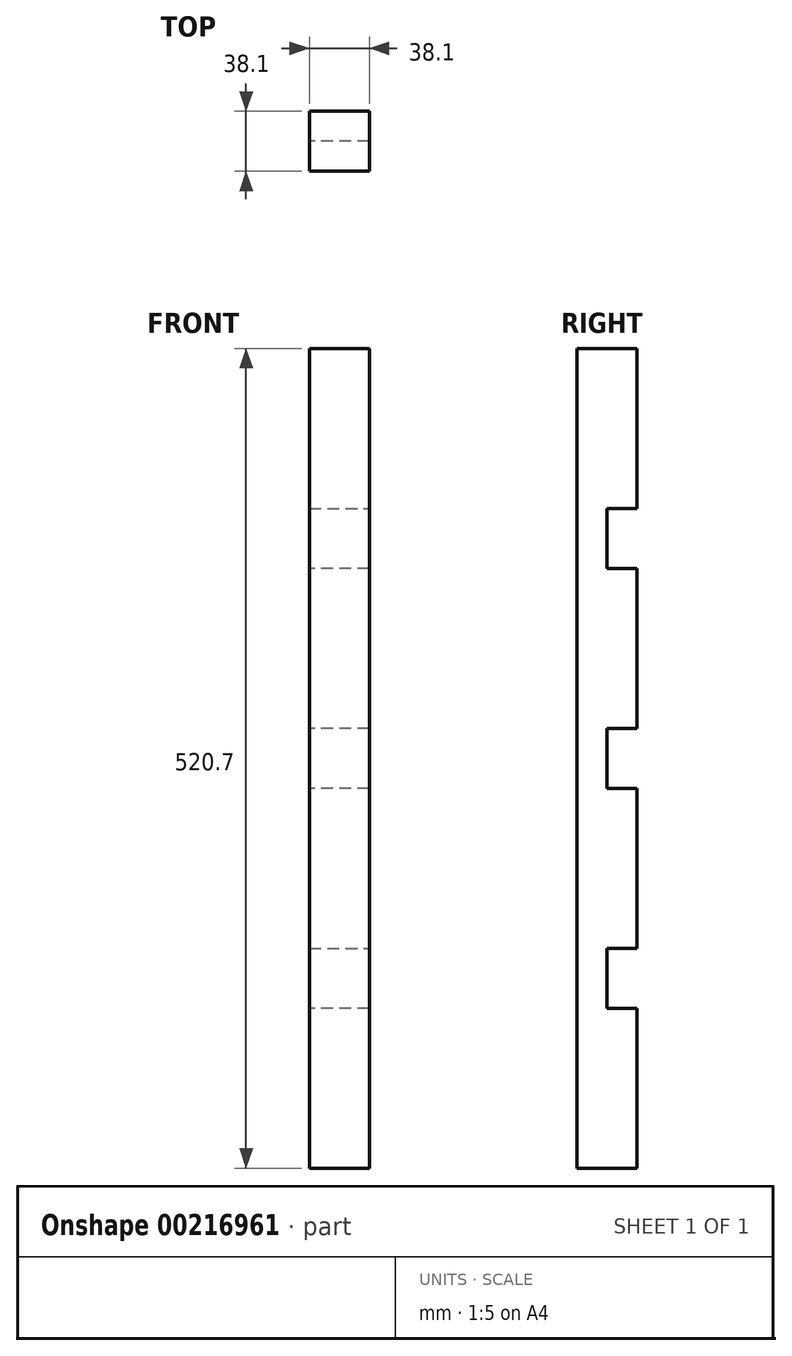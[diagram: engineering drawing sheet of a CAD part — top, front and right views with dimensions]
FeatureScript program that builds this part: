
annotation { "Feature Type Name" : "Feature", "Feature Type Description" : "" }
export const myFeature = defineFeature(function(context is Context, id is Id, definition is map)
    precondition{}
    {
        {
            var Q0;
            Q0=qCreatedBy(makeId("Top.planeOp"),FACE);
            var sketch = newSketch(context, id + "F0", { "sketchPlane" : qUnion([Q0])});
            skLineSegment(sketch, "E0", {"start": v(0, 0) * mm, "end": v(-50.8, 0) * mm});
            skLineSegment(sketch, "E1", {"start": v(0, 0) * mm, "end": v(50.8, 0) * mm});
            skLineSegment(sketch, "E2", {"start": v(50.8, 0) * mm, "end": v(50.8, 38.1) * mm});
            skLineSegment(sketch, "E3", {"start": v(88.9, 38.1) * mm, "end": v(88.9, 0) * mm});
            skLineSegment(sketch, "E4", {"start": v(88.9, 0) * mm, "end": v(190.5, 0) * mm});
            skLineSegment(sketch, "E5", {"start": v(190.5, 0) * mm, "end": v(190.5, 38.1) * mm});
            skLineSegment(sketch, "E6", {"start": v(-50.8, 0) * mm, "end": v(-50.8, 38.1) * mm});
            skLineSegment(sketch, "E7", {"start": v(-88.9, 38.1) * mm, "end": v(-190.5, 38.1) * mm});
            skLineSegment(sketch, "E8", {"start": v(-190.5, 38.1) * mm, "end": v(-190.5, 0) * mm});
            skLineSegment(sketch, "E9", {"start": v(-228.6, 0) * mm, "end": v(-228.6, 38.1) * mm});
            skLineSegment(sketch, "E10", {"start": v(-228.6, 38.1) * mm, "end": v(-330.2, 38.1) * mm});
            skLineSegment(sketch, "E11", {"start": v(-330.2, 38.1) * mm, "end": v(-330.2, 0) * mm});
            skLineSegment(sketch, "E12", {"start": v(-88.9, 0) * mm, "end": v(-88.9, 38.1) * mm});
            skLineSegment(sketch, "E13.trimOffspring", {"start": v(-330.2, 38.1) * mm, "end": v(-228.6, 38.1) * mm});
            skLineSegment(sketch, "E14.trimOffspring", {"start": v(-190.5, 38.1) * mm, "end": v(-88.9, 38.1) * mm});
            skLineSegment(sketch, "E15.trimOffspring", {"start": v(-228.6, 0) * mm, "end": v(-330.2, 0) * mm});
            skLineSegment(sketch, "E16.trimOffspring", {"start": v(-88.9, 0) * mm, "end": v(-190.5, 0) * mm});
            skLineSegment(sketch, "E17.trimOffspring", {"start": v(-50.8, 38.1) * mm, "end": v(50.8, 38.1) * mm});
            skLineSegment(sketch, "E18.trimOffspring", {"start": v(50.8, 0) * mm, "end": v(0, 0) * mm});
            skLineSegment(sketch, "E19.trimOffspring", {"start": v(88.9, 38.1) * mm, "end": v(190.5, 38.1) * mm});
            skLineSegment(sketch, "E20.trimOffspring", {"start": v(190.5, 0) * mm, "end": v(88.9, 0) * mm});
            skLineSegment(sketch, "E21", {"start": v(-88.9, -135.66) * mm, "end": v(-69.85, -135.66) * mm, "construction": true});
            skLineSegment(sketch, "E22", {"start": v(-69.85, -135.66) * mm, "end": v(-69.85, 272.84) * mm, "construction": true});
            skSolve(sketch);
        }
        {
            var Q0;
            Q0=qSketchRegion(id+"F0",true);
            extrude(context, id + "F1", {"entities" : qUnion([Q0]), "depth" : 19.05 * mm});
        }
        {
            var Q0;
            Q0=makeQuery(id+"F1.opExtrude","CAP_FACE",FACE,{"disambiguationData":[OSD([sQuery(id+"F0.wireOp",EDGE,"E9"),sQuery(id+"F0.wireOp",EDGE,"E11"),sQuery(id+"F0.wireOp",EDGE,"E13.trimOffspring"),sQuery(id+"F0.wireOp",EDGE,"E15.trimOffspring")])],"isStart":false});
            var sketch = newSketch(context, id + "F2", { "sketchPlane" : qUnion([Q0])});
            skLineSegment(sketch, "E23.bottom", {"start": v(-330.2, 0) * mm, "end": v(190.5, 0) * mm});
            skLineSegment(sketch, "E23.top", {"start": v(-330.2, 38.1) * mm, "end": v(190.5, 38.1) * mm});
            skLineSegment(sketch, "E23.left", {"start": v(-330.2, 0) * mm, "end": v(-330.2, 38.1) * mm});
            skLineSegment(sketch, "E23.right", {"start": v(190.5, 0) * mm, "end": v(190.5, 38.1) * mm});
            skSolve(sketch);
        }
        {
            var Q0;
            Q0=qSketchRegion(id+"F2",true);
            extrude(context, id + "F3", {"entities" : qUnion([Q0]), "depth" : 19.05 * mm});
        }
        {
            var Q0;
            Q0=makeQuery(id+"F3.opExtrude","SWEPT_BODY",BODY,{"disambiguationData":[OSD([sQuery(id+"F2.wireOp",EDGE,"E23.bottom"),sQuery(id+"F2.wireOp",EDGE,"E23.top"),sQuery(id+"F2.wireOp",EDGE,"E23.left"),sQuery(id+"F2.wireOp",EDGE,"E23.right")])]});
            var Q1;
            Q1=makeQuery(id+"F1.opExtrude","SWEPT_BODY",BODY,{"disambiguationData":[OSD([sQuery(id+"F0.wireOp",EDGE,"E2"),sQuery(id+"F0.wireOp",EDGE,"E0"),sQuery(id+"F0.wireOp",EDGE,"E6"),sQuery(id+"F0.wireOp",EDGE,"E17.trimOffspring"),sQuery(id+"F0.wireOp",EDGE,"E18.trimOffspring")])]});
            var Q2;
            Q2=makeQuery(id+"F1.opExtrude","SWEPT_BODY",BODY,{"disambiguationData":[OSD([sQuery(id+"F0.wireOp",EDGE,"E3"),sQuery(id+"F0.wireOp",EDGE,"E5"),sQuery(id+"F0.wireOp",EDGE,"E19.trimOffspring"),sQuery(id+"F0.wireOp",EDGE,"E20.trimOffspring")])]});
            var Q3;
            Q3=makeQuery(id+"F1.opExtrude","SWEPT_BODY",BODY,{"disambiguationData":[OSD([sQuery(id+"F0.wireOp",EDGE,"E8"),sQuery(id+"F0.wireOp",EDGE,"E12"),sQuery(id+"F0.wireOp",EDGE,"E14.trimOffspring"),sQuery(id+"F0.wireOp",EDGE,"E16.trimOffspring")])]});
            var Q4;
            Q4=makeQuery(id+"F1.opExtrude","SWEPT_BODY",BODY,{"disambiguationData":[OSD([sQuery(id+"F0.wireOp",EDGE,"E9"),sQuery(id+"F0.wireOp",EDGE,"E11"),sQuery(id+"F0.wireOp",EDGE,"E13.trimOffspring"),sQuery(id+"F0.wireOp",EDGE,"E15.trimOffspring")])]});
            booleanBodies(context, id + "F4", {"operationType" : BooleanOperationType.UNION, "tools" : qUnion([Q0, Q1, Q2, Q3, Q4])});
        }
        {
            var Q0;
            Q0=makeQuery(id+"F3.opExtrude","SWEPT_BODY",BODY,{"disambiguationData":[OSD([sQuery(id+"F2.wireOp",EDGE,"E23.bottom"),sQuery(id+"F2.wireOp",EDGE,"E23.top"),sQuery(id+"F2.wireOp",EDGE,"E23.left"),sQuery(id+"F2.wireOp",EDGE,"E23.right")])]});
            var Q1;
            Q1=makeQuery(id+"F3.opExtrude","CAP_EDGE",EDGE,{"disambiguationData":[OSD([sQuery(id+"F2.wireOp",EDGE,"E23.left")])],"isStart":false});
            transform(context, id + "F5", {"entities" : qUnion([Q0]), "transformType" : TransformType.ROTATION, "transformAxis" : qUnion([Q1]), "angle" : 90 * degree, "makeCopy" : false});
        }
        {
            var Q0;
            Q0=makeQuery(id+"F3.opExtrude","SWEPT_BODY",BODY,{"disambiguationData":[OSD([sQuery(id+"F2.wireOp",EDGE,"E23.bottom"),sQuery(id+"F2.wireOp",EDGE,"E23.top"),sQuery(id+"F2.wireOp",EDGE,"E23.left"),sQuery(id+"F2.wireOp",EDGE,"E23.right")])]});
            var Q1;
            Q1=makeQuery(id+"F3.opExtrude","CAP_EDGE",EDGE,{"disambiguationData":[OSD([sQuery(id+"F2.wireOp",EDGE,"E23.top")])],"isStart":false});
            transform(context, id + "F6", {"entities" : qUnion([Q0]), "transformType" : TransformType.ROTATION, "transformAxis" : qUnion([Q1]), "angle" : 90 * degree, "makeCopy" : false});
        }
    });
